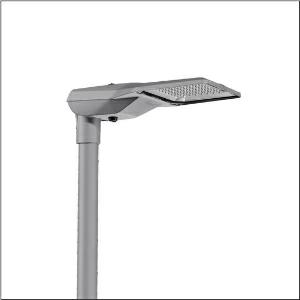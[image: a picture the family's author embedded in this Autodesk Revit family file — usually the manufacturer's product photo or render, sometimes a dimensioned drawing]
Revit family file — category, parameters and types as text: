
# Revit family: streetlight_sl_21_iq_midi___st1_0a_5xe3d61y08mb_8671
name_source: partatom
category: Lighting Fixtures
units: mm (PartAtom-declared; Revit-internal decimal feet)

## family parameters
Cut with Voids When Loaded = No
Host = Face
Light Source = No
Part Type = Normal
Room Calculation Point = No
Round Connector Dimension = Use Diameter
Shared = No

## types (1)
- --- (1 x LED, 15910 lm, 129.3 W, 2700K)
    Apparent Load = 129 VA
    CIE Flux Codes = 37 72 97 100 100
    Color Rendering = 70
    Color Temperature = 2700K
    Default Elevation = 1800 mm
    Description = Streetlight SL 21 iQ midi, mast luminaire, primary light control with lens, of PMMA, primary optical cover: cover, of toughened safety glass, transparent, light distribution: ST1.0a, light emission: direct distribution, primary light characteristic: asymmetric, installation type: post-top, side-entry, LED, High Power LED, rated luminous flux: 15.910lm, luminous efficacy: 123lm/W, light colour: 727, colour temperature: 2700K, control: presetting dimming logarithmic, Street-Remote, Auto-Match, Temp-Guard, Lumen-Switch, Night-Set, Smart-Wire, Light-Fading, Desk-Remote (wireless, voltage-free reading and setting of iQ features in the workshop via application-optimized NFC function/RFID function), optimised constant luminous flux control (CLO 2.0), mains connection: 230..240V, AC, 50/60Hz, start of lifetime: 129W, end of service life: 142W, reduction: 56W, luminaire housing, of diecast aluminium, powder-coated, Siteco® metallic grey (DB 702S), corrosivity category C5 mid according to DIN EN ISO 12944, please order mast flange separately, inclination adjustable: 0°, 5°, 10°, 15°, sealing non-destructively replaceable, multi-level sealing system, length: 644mm, width: 335mm, height: 110mm, mast flange for spigot size: 42mm (side-entry): 5XC10008XM4, 60/48mm (side-entry/post-top): 5XC10108XM2, 76/60mm (side-entry/post-top): 5XC10108XM1, Smart Interface below and above, protection rating (complete): IP66, insulation class (complete): insulation class II (safety insulation), certification: CE, ENEC, ENEC+, VDE, impact resistance: IK09, permissible operating ambient temperature for outdoor applications: -40..+50°C, standard-compliant lighting for roads and squares, packaging unit: 1 piece

Light Distribution: ST1.0a
    Height = 111 mm
    Lamp = 1 x LED
    Lamp Light Flux = 15910 lm
    Lamp Power = 129.3 W
    Lamp count = 1
    Length = 644 mm
    Luminous efficacy = 123 lm/W
    Manufacturer = Siteco
    ModVariant = No
    Model = 5XE3D61Y08MB
    Number of Poles = 1
    OnlyDefault = Yes
    Power Factor = 1
    Product Name = Streetlight SL 21 iQ midi | ST1.0a
    Product group = mast luminaire | pylon top
    ProductGroupID = 6100
    Protection Class = Protection class II
    Protection Degree = IP 66
    RLX_Detail_Level = 1
    RLX_Emergency_Light_Flux = 0 lm
    RLX_Emergency_Type = 0
    RLX_Emergency_Type_DB = No
    RlxData = <blob elided: 91201 chars, md5=bcfd9234>
    Socket = socket
    Standby Power = 0 W
    System Light Flux = 15910 lm
    System Power = 129 W
    Type Comments = factory setting: luminous flux: 100 % | dim-lin: 254 | 672 mA
    Type Image = l_1004304.jpg
    URL = http://relux.com
    VarID = @adj_044607
    Voltage = 0 V
    Weight = 0.00 kg
    Width = 336 mm

## geometry (parser evidence)
native form markers: Blend x4, Sweep x12
no freeform markers — native parametric forms only
